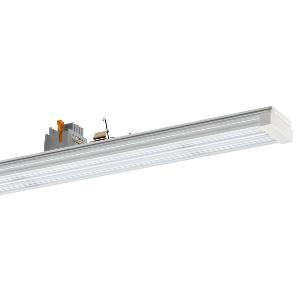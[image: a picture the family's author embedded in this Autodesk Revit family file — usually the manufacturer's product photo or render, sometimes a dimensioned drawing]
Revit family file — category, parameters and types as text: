
# Revit family: conveo_-_cvg_15000_850_xn-p_da_7_226848189-00804956_818b
name_source: partatom
category: Lighting Fixtures
units: mm (PartAtom-declared; Revit-internal decimal feet)

## family parameters
Cut with Voids When Loaded = No
Host = Face
Light Source = No
Part Type = Normal
Room Calculation Point = No
Round Connector Dimension = Use Diameter
Shared = No

## types (1)
- CONVEO - CVG 15000/850/xN-P/DA/7 (1 x LED, 14200 lm, 5000K)
    Apparent Load = 100 VA
    Approval mark = CE
    CIE Flux Codes = 57 84 97 100 100
    Color Rendering = 80-89
    Color Temperature = 5000K
    Control Gear = Electronic ballast
    Default Elevation = 1800 mm
    Description = CVG 15000/850/xN-P/DA/7|Continuous-row system|light source: LED|work equipment: Adjustable electronic ballast, digital DALI|connected load: 220-240 V, 50-60 Hz|Power consumption: approx. 100 W|luminous flux: 14200 lm|luminous efficacy: 142 lm/W|colour temperature: Cold white, ca. 5000 K|color rendering index (CRI): >= 80|chromaticity tolerance:  3 SDCM|System of protection: IP 54|class of protection: I|technology: Continuously dimmable|luminaire body|material: Aluminium|surface: Powder coatet|colour: White|lamp cover: Acrylic (PMMA), Satine|weight (net): approx. 2.2 kg|Fastening: Available separately|minimum ambient temperature: -25 ░C|maximum ambient temperature: 33 ░C|glare control: Prism optics (linear)|Approval mark: VDE - ENEC|
    Frequency = 50 Hz
    Height = 70 mm
    Lamp = 1 x LED
    Lamp Light Flux = 14200 lm
    Lamp count = 1
    Length = 1500 mm
    Luminous efficacy = 142 lm/W
    Manufacturer = Waldmann
    ModVariant = No
    Model = 226848189-00804956
    Mounting Place = Ceiling
    Mounting Type = Pendant
    Number of Poles = 1
    OnlyDefault = Yes
    Power Factor = 1
    Product Name = CONVEO - CVG 15000/850/xN-P/DA/7
    Product group = Continuous-row system (industry)
    ProductGroupID = 301
    Protection Class = Protection class I
    Protection Degree = IP 54
    RLX_Detail_Level = 1
    RlxData = <blob elided: 133673 chars, md5=614644b8>
    Socket = socket
    Standby Power = 0 W
    System Light Flux = 14200 lm
    System Power = 100 W
    Type Comments = Product without accessories
    Type Image = 226848059-00804941-2p7.jpg
    URL = http://relux.com
    VarID = ---
    Voltage = 230 V
    Voltage Range = 220-240 V
    Weight = 0.00 kg
    Width = 64 mm

## geometry (parser evidence)
native form markers: Blend x4, Sweep x9
no freeform markers — native parametric forms only
